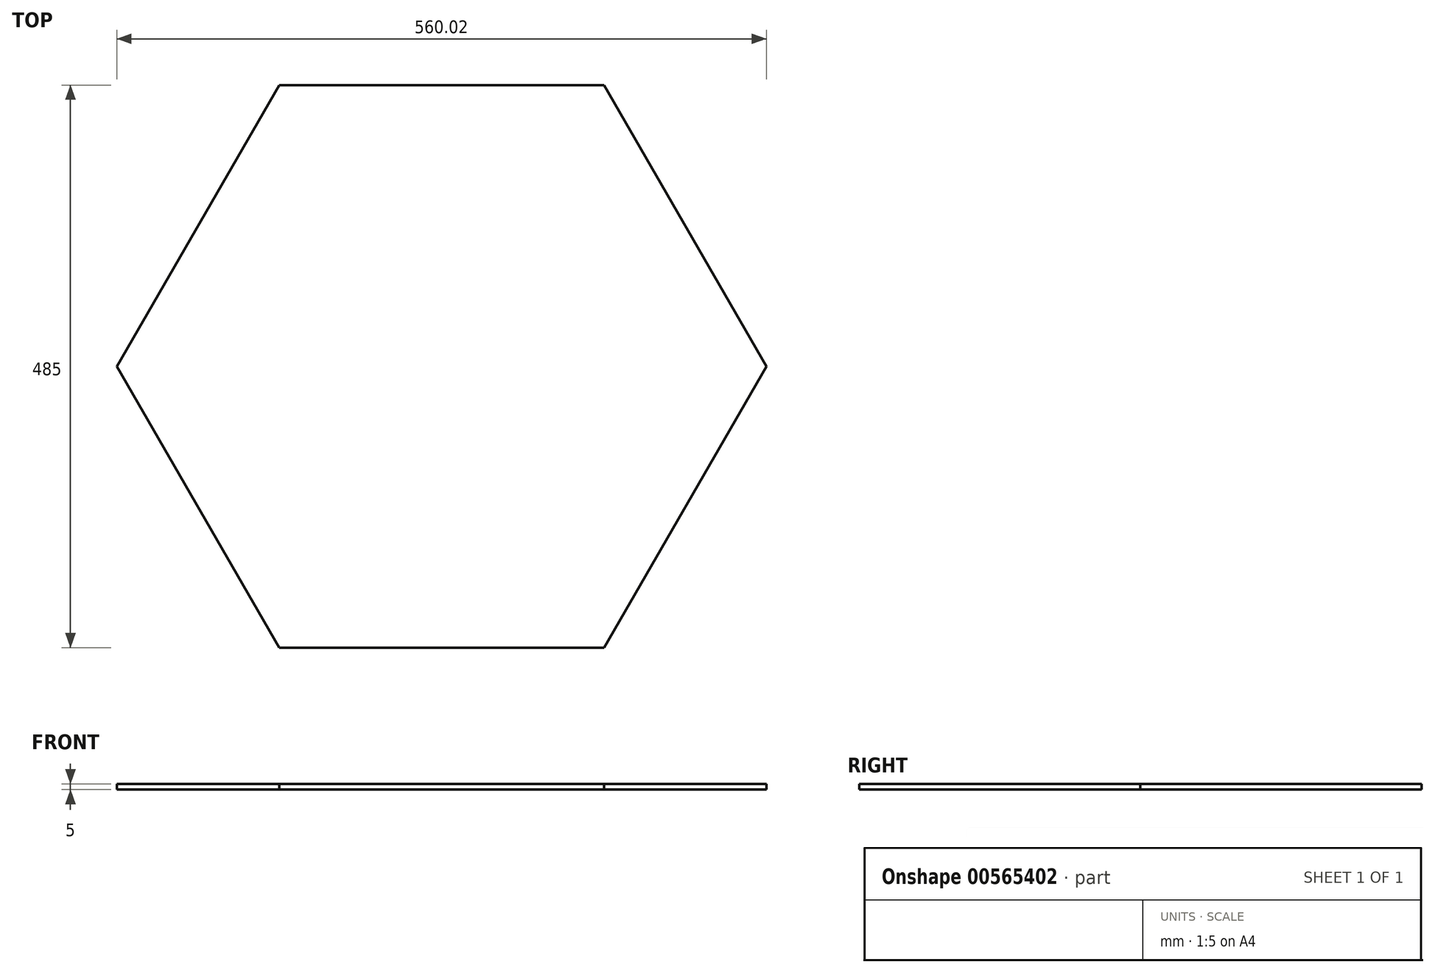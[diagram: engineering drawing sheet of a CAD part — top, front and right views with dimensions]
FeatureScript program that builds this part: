
annotation { "Feature Type Name" : "Feature", "Feature Type Description" : "" }
export const myFeature = defineFeature(function(context is Context, id is Id, definition is map)
    precondition{}
    {
        {
            var Q0;
            Q0=qCreatedBy(makeId("Top.planeOp"),FACE);
            var sketch = newSketch(context, id + "F0", { "sketchPlane" : qUnion([Q0])});
            skCircle(sketch, "E0.cCircle", {"center": v(0, 0) * mm, "radius": 242.5 * mm, "construction": true});
            skLineSegment(sketch, "E0.0", {"start": v(140, -242.5) * mm, "end": v(-140, -242.5) * mm});
            skLineSegment(sketch, "E0.1", {"start": v(-140, -242.5) * mm, "end": v(-280.01, 0) * mm});
            skLineSegment(sketch, "E0.2", {"start": v(-280.01, 0) * mm, "end": v(-140, 242.5) * mm});
            skLineSegment(sketch, "E0.3", {"start": v(-140, 242.5) * mm, "end": v(140, 242.5) * mm});
            skLineSegment(sketch, "E0.4", {"start": v(140, 242.5) * mm, "end": v(280.01, 0) * mm});
            skLineSegment(sketch, "E0.5", {"start": v(280.01, 0) * mm, "end": v(140, -242.5) * mm});
            skPoint(sketch, "E0.0.midPoint", {"position": v(0, -242.5) * mm});
            skSolve(sketch);
        }
        {
            var Q0;
            Q0=makeQuery(id+"F0.imprint","IMPRINT",FACE,{"disambiguationData":[TD([[makeQuery(id+"F0.imprint","IMPRINT",EDGE,{"derivedFrom":sQuery(id+"F0.wireOp",EDGE,"E0.0")}),-1.0]])]});
            extrude(context, id + "F1", {"entities" : qUnion([Q0]), "depth" : 5 * mm, "offsetDistance" : 25 * mm});
        }
    });
